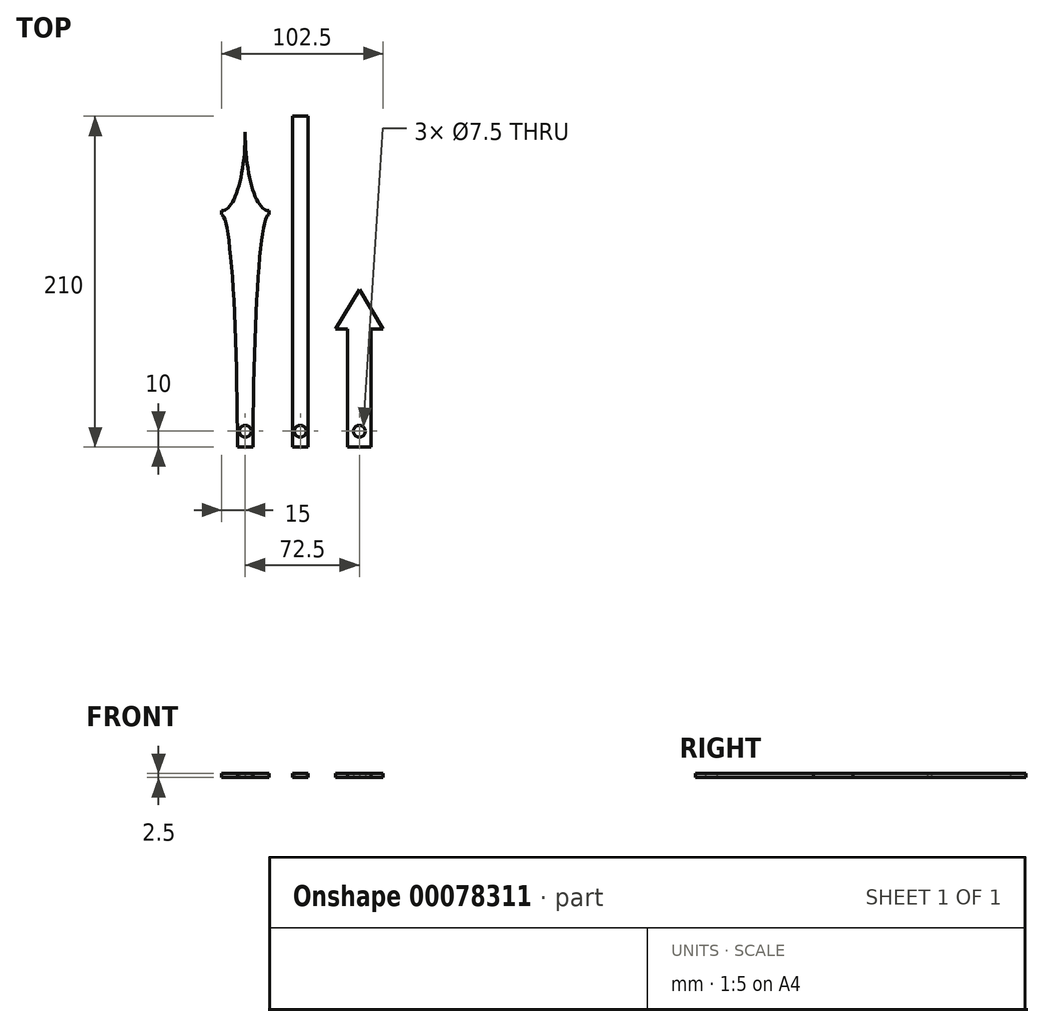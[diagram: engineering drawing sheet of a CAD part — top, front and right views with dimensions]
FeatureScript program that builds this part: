
annotation { "Feature Type Name" : "Feature", "Feature Type Description" : "" }
export const myFeature = defineFeature(function(context is Context, id is Id, definition is map)
    precondition{}
    {
        {
            var Q0;
            Q0=qCreatedBy(makeId("Top.planeOp"),FACE);
            var sketch = newSketch(context, id + "F0", { "sketchPlane" : qUnion([Q0])});
            skLineSegment(sketch, "E0", {"start": v(0, 0) * mm, "end": v(0, 150) * mm});
            skLineSegment(sketch, "E1", {"start": v(0, 150) * mm, "end": v(15, 150) * mm});
            skLineSegment(sketch, "E2", {"start": v(0, 150) * mm, "end": v(0, 200) * mm});
            skLineSegment(sketch, "E3", {"start": v(0, 0) * mm, "end": v(5, 0) * mm});
            skLineSegment(sketch, "E4", {"start": v(5, 0) * mm, "end": v(5, 75) * mm});
            skLineSegment(sketch, "E5.0", {"start": v(5, 147.5) * mm, "end": v(15, 147.5) * mm});
            skEllipticalArc(sketch, "E6", {});
            skLineSegment(sketch, "E7", {"start": v(15, 147.5) * mm, "end": v(15, 150) * mm});
            skEllipticalArc(sketch, "E8", {});
            skPoint(sketch, "E9.orphan", {"position": v(5, 200) * mm});
            skPoint(sketch, "E10.orphan", {"position": v(0, 147.5) * mm});
            skLineSegment(sketch, "E11.trimOffspring", {"start": v(5, 147.5) * mm, "end": v(5, 150) * mm});
            skEllipticalArc(sketch, "E12.MirrorCS", {});
            skEllipticalArc(sketch, "E13.MirrorCS", {});
            skLineSegment(sketch, "E14.MirrorCS", {"start": v(-15, 147.5) * mm, "end": v(-15, 150) * mm});
            skLineSegment(sketch, "E15.MirrorCS", {"start": v(0, 0) * mm, "end": v(-5, 0) * mm});
            skCircle(sketch, "E16", {"center": v(0, 10) * mm, "radius": 3.75 * mm});
            const initialGuessF0  = {"E6": [0.015, 0, 0, -1, 0.1475, 0.01, 3.141592653589793, 4.71238898038469], "E8": [0.015, 0.2, -1, 0, 0.015, 0.05, 6.283185307179586, 1.5707963267948966], "E12.MirrorCS": [-0.015, 0.2, 1, 0, 0.015, 0.05, 4.71238898038469, 6.283185307179586], "E13.MirrorCS": [-0.015, 0, 0, -1, 0.1475, 0.01, 1.5707963267948966, 3.141592653589793]};
            skSetInitialGuess(sketch, initialGuessF0);
            skSolve(sketch);
        }
        {
            var Q0;
            {var subQ0=sQuery(id+"F0.wireOp",EDGE,"E3");Q0=makeQuery(id+"F0.imprint","IMPRINT",FACE,{"disambiguationData":[TD([[makeQuery(id+"F0.imprint","IMPRINT",EDGE,{"derivedFrom":subQ0}),1.0]])]});}
            var Q1;
            Q1=makeQuery(id+"F0.imprint","IMPRINT",FACE,{"disambiguationData":[TD([[makeQuery(id+"F0.imprint","IMPRINT",EDGE,{"derivedFrom":sQuery(id+"F0.wireOp",EDGE,"E5.0")}),1.0]])]});
            var Q2;
            {var subQ0=sQuery(id+"F0.wireOp",EDGE,"E2");Q2=makeQuery(id+"F0.imprint","IMPRINT",FACE,{"disambiguationData":[TD([[makeQuery(id+"F0.imprint","IMPRINT",EDGE,{"derivedFrom":subQ0}),-1.0]])]});}
            var Q3;
            {var subQ0=sQuery(id+"F0.wireOp",EDGE,"E2");Q3=makeQuery(id+"F0.imprint","IMPRINT",FACE,{"disambiguationData":[TD([[makeQuery(id+"F0.imprint","IMPRINT",EDGE,{"derivedFrom":subQ0}),1.0]])]});}
            extrude(context, id + "F1", {"entities" : qUnion([Q0, Q1, Q2, Q3]), "depth" : 2.5 * mm});
        }
        {
            var Q0;
            Q0=qCreatedBy(makeId("Top.planeOp"),FACE);
            var sketch = newSketch(context, id + "F2", { "sketchPlane" : qUnion([Q0])});
            skLineSegment(sketch, "E17", {"start": v(30, 0) * mm, "end": v(40, 0) * mm});
            skLineSegment(sketch, "E18", {"start": v(40, 0) * mm, "end": v(40, 210) * mm});
            skLineSegment(sketch, "E19", {"start": v(30, 0) * mm, "end": v(30, 210) * mm});
            skLineSegment(sketch, "E20", {"start": v(30, 210) * mm, "end": v(40, 210) * mm});
            skLineSegment(sketch, "E21", {"start": v(0, 0) * mm, "end": v(30, 0) * mm});
            skCircle(sketch, "E22", {"center": v(35, 10) * mm, "radius": 3.75 * mm});
            skLineSegment(sketch, "E23", {"start": v(35, 0) * mm, "end": v(35, 10) * mm, "construction": true});
            skSolve(sketch);
        }
        {
            var Q0;
            Q0 = qSketchRegion(id + "F2", true);
            extrude(context, id + "F3", {"entities" : qUnion([Q0]), "depth" : 2.5 * mm});
        }
        {
            var Q0;
            Q0=qCreatedBy(makeId("Top.planeOp"),FACE);
            var sketch = newSketch(context, id + "F4", { "sketchPlane" : qUnion([Q0])});
            skLineSegment(sketch, "E24", {"start": v(65, 0) * mm, "end": v(80, 0) * mm});
            skLineSegment(sketch, "E25", {"start": v(65, 0) * mm, "end": v(65, 75) * mm});
            skLineSegment(sketch, "E26", {"start": v(65, 75) * mm, "end": v(57.5, 75) * mm});
            skLineSegment(sketch, "E27", {"start": v(57.5, 75) * mm, "end": v(72.5, 100) * mm});
            skLineSegment(sketch, "E28", {"start": v(72.5, 100) * mm, "end": v(72.5, 0) * mm, "construction": true});
            skPoint(sketch, "E28.endSnap0", {"position": v(72.5, 0) * mm});
            skLineSegment(sketch, "E29", {"start": v(0, 0) * mm, "end": v(65, 0) * mm});
            skLineSegment(sketch, "E30.MirrorCS", {"start": v(80, 0) * mm, "end": v(80, 75) * mm});
            skLineSegment(sketch, "E31.MirrorCS", {"start": v(87.5, 75) * mm, "end": v(72.5, 100) * mm});
            skLineSegment(sketch, "E32.MirrorCS", {"start": v(80, 75) * mm, "end": v(87.5, 75) * mm});
            skCircle(sketch, "E33", {"center": v(72.5, 10) * mm, "radius": 3.75 * mm});
            skSolve(sketch);
        }
        {
            var Q0;
            Q0 = qSketchRegion(id + "F4", true);
            extrude(context, id + "F5", {"entities" : qUnion([Q0]), "depth" : 2.5 * mm});
        }
    });
